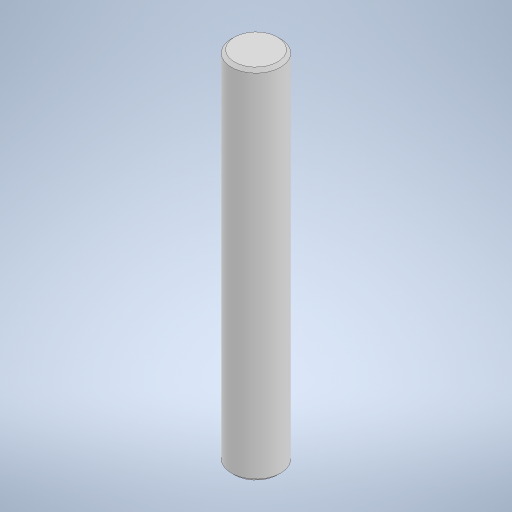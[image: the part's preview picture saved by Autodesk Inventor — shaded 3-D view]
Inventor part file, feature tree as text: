
AUTODESK INVENTOR PART (.ipt)
format: ipt  version: 2023.1 (Build 271208000, 208)  size: 228,352 bytes
history: native  units: in
note: dims shown in document units (in); Inventor stores cm internally (conversion verified against a paired STEP export)
features: extrude x1, chamfer x1, sketch x1
ambient origin geometry x8: Origin, YZ Plane, XZ Plane, XY Plane, X Axis, Y Axis, Z Axis, Center Point
bodies: Solid1 (feature_tree)
feature tree (3):
  extrude  "Extrusion1"  Depth=1.1417in TaperAngle=0.0deg
  chamfer  "Chamfer1"  Distance=0.0098in Angle=45.0deg
  sketch  "Sketch1"  dims[d0=0.1575in d1=1.1417in d2=0.0in d3=0.0098in d4=0.125in d5=45.0deg]
